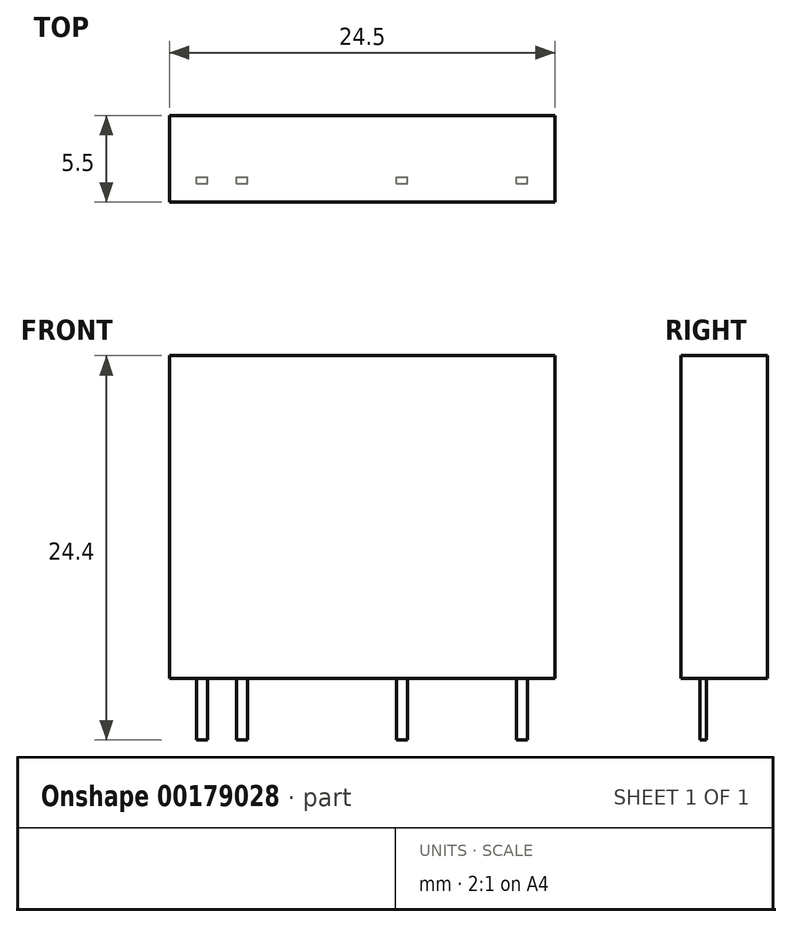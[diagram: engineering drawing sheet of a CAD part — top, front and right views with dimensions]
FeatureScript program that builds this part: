
annotation { "Feature Type Name" : "Feature", "Feature Type Description" : "" }
export const myFeature = defineFeature(function(context is Context, id is Id, definition is map)
    precondition{}
    {
        {
            var Q0;
            Q0=qCreatedBy(makeId("Top.planeOp"),FACE);
            var sketch = newSketch(context, id + "F0", { "sketchPlane" : qUnion([Q0])});
            skLineSegment(sketch, "E0.bottom", {"start": v(-12.25, 2.75) * mm, "end": v(12.25, 2.75) * mm});
            skLineSegment(sketch, "E0.top", {"start": v(-12.25, -2.75) * mm, "end": v(12.25, -2.75) * mm});
            skLineSegment(sketch, "E0.left", {"start": v(-12.25, 2.75) * mm, "end": v(-12.25, -2.75) * mm});
            skLineSegment(sketch, "E0.right", {"start": v(12.25, 2.75) * mm, "end": v(12.25, -2.75) * mm});
            skLineSegment(sketch, "E1.bottom", {"start": v(-10.5, -1.55) * mm, "end": v(-9.81, -1.55) * mm});
            skLineSegment(sketch, "E1.top", {"start": v(-10.5, -1.15) * mm, "end": v(-9.81, -1.15) * mm});
            skLineSegment(sketch, "E1.left", {"start": v(-10.5, -1.55) * mm, "end": v(-10.5, -1.15) * mm});
            skLineSegment(sketch, "E1.right", {"start": v(-9.8, -1.55) * mm, "end": v(-9.8, -1.15) * mm});
            skPoint(sketch, "E2", {"position": v(-10.16, -1.35) * mm});
            skLineSegment(sketch, "E3", {"start": v(-12.25, -1.35) * mm, "end": v(12.25, -1.35) * mm, "construction": true});
            skPoint(sketch, "E4", {"position": v(-7.62, -1.35) * mm});
            skPoint(sketch, "E5", {"position": v(2.54, -1.35) * mm});
            skPoint(sketch, "E6", {"position": v(10.16, -1.35) * mm});
            skLineSegment(sketch, "E7", {"start": v(-10.16, -1.55) * mm, "end": v(-10.16, -1.15) * mm, "construction": true});
            skLineSegment(sketch, "E8.bottom", {"start": v(-7.97, -1.55) * mm, "end": v(-7.27, -1.55) * mm});
            skLineSegment(sketch, "E8.top", {"start": v(-7.97, -1.15) * mm, "end": v(-7.27, -1.15) * mm});
            skLineSegment(sketch, "E8.left", {"start": v(-7.97, -1.55) * mm, "end": v(-7.97, -1.15) * mm});
            skLineSegment(sketch, "E8.right", {"start": v(-7.27, -1.55) * mm, "end": v(-7.27, -1.15) * mm});
            skLineSegment(sketch, "E9.bottom", {"start": v(2.2, -1.55) * mm, "end": v(2.9, -1.55) * mm});
            skLineSegment(sketch, "E9.top", {"start": v(2.2, -1.15) * mm, "end": v(2.9, -1.15) * mm});
            skLineSegment(sketch, "E9.left", {"start": v(2.2, -1.55) * mm, "end": v(2.2, -1.15) * mm});
            skLineSegment(sketch, "E9.right", {"start": v(2.9, -1.55) * mm, "end": v(2.9, -1.15) * mm});
            skLineSegment(sketch, "E10.bottom", {"start": v(9.8, -1.55) * mm, "end": v(10.5, -1.55) * mm});
            skLineSegment(sketch, "E10.top", {"start": v(9.8, -1.15) * mm, "end": v(10.5, -1.15) * mm});
            skLineSegment(sketch, "E10.left", {"start": v(9.8, -1.55) * mm, "end": v(9.8, -1.15) * mm});
            skLineSegment(sketch, "E10.right", {"start": v(10.5, -1.55) * mm, "end": v(10.5, -1.15) * mm});
            skLineSegment(sketch, "E11", {"start": v(-7.62, -1.55) * mm, "end": v(-7.62, -1.15) * mm, "construction": true});
            skLineSegment(sketch, "E12", {"start": v(2.54, -1.55) * mm, "end": v(2.54, -1.15) * mm, "construction": true});
            skLineSegment(sketch, "E13", {"start": v(10.16, -1.55) * mm, "end": v(10.16, -1.15) * mm, "construction": true});
            skSolve(sketch);
        }
        {
            var Q0;
            Q0=makeQuery(id+"F0.imprint","IMPRINT",FACE,{"disambiguationData":[TD([[makeQuery(id+"F0.imprint","IMPRINT",EDGE,{"derivedFrom":sQuery(id+"F0.wireOp",EDGE,"E1.bottom")}),1.0]])]});
            var Q1;
            Q1=makeQuery(id+"F0.imprint","IMPRINT",FACE,{"disambiguationData":[TD([[makeQuery(id+"F0.imprint","IMPRINT",EDGE,{"derivedFrom":sQuery(id+"F0.wireOp",EDGE,"E0.bottom")}),-1.0]])]});
            var Q2;
            Q2=makeQuery(id+"F0.imprint","IMPRINT",FACE,{"disambiguationData":[TD([[makeQuery(id+"F0.imprint","IMPRINT",EDGE,{"derivedFrom":sQuery(id+"F0.wireOp",EDGE,"E9.bottom")}),1.0]])]});
            var Q3;
            Q3=makeQuery(id+"F0.imprint","IMPRINT",FACE,{"disambiguationData":[TD([[makeQuery(id+"F0.imprint","IMPRINT",EDGE,{"derivedFrom":sQuery(id+"F0.wireOp",EDGE,"E10.bottom")}),1.0]])]});
            var Q4;
            Q4=makeQuery(id+"F0.imprint","IMPRINT",FACE,{"disambiguationData":[TD([[makeQuery(id+"F0.imprint","IMPRINT",EDGE,{"derivedFrom":sQuery(id+"F0.wireOp",EDGE,"E8.bottom")}),1.0]])]});
            extrude(context, id + "F1", {"entities" : qUnion([Q0, Q1, Q2, Q3, Q4]), "depth" : 20.5 * mm});
        }
        {
            var Q0;
            Q0=makeQuery(id+"F0.imprint","IMPRINT",FACE,{"disambiguationData":[TD([[makeQuery(id+"F0.imprint","IMPRINT",EDGE,{"derivedFrom":sQuery(id+"F0.wireOp",EDGE,"E1.bottom")}),1.0]])]});
            var Q1;
            Q1=makeQuery(id+"F0.imprint","IMPRINT",FACE,{"disambiguationData":[TD([[makeQuery(id+"F0.imprint","IMPRINT",EDGE,{"derivedFrom":sQuery(id+"F0.wireOp",EDGE,"E8.bottom")}),1.0]])]});
            var Q2;
            Q2=makeQuery(id+"F0.imprint","IMPRINT",FACE,{"disambiguationData":[TD([[makeQuery(id+"F0.imprint","IMPRINT",EDGE,{"derivedFrom":sQuery(id+"F0.wireOp",EDGE,"E9.bottom")}),1.0]])]});
            var Q3;
            Q3=makeQuery(id+"F0.imprint","IMPRINT",FACE,{"disambiguationData":[TD([[makeQuery(id+"F0.imprint","IMPRINT",EDGE,{"derivedFrom":sQuery(id+"F0.wireOp",EDGE,"E10.bottom")}),1.0]])]});
            extrude(context, id + "F2", {"entities" : qUnion([Q0, Q1, Q2, Q3]), "oppositeDirection" : true, "depth" : 3.9 * mm});
        }
    });
